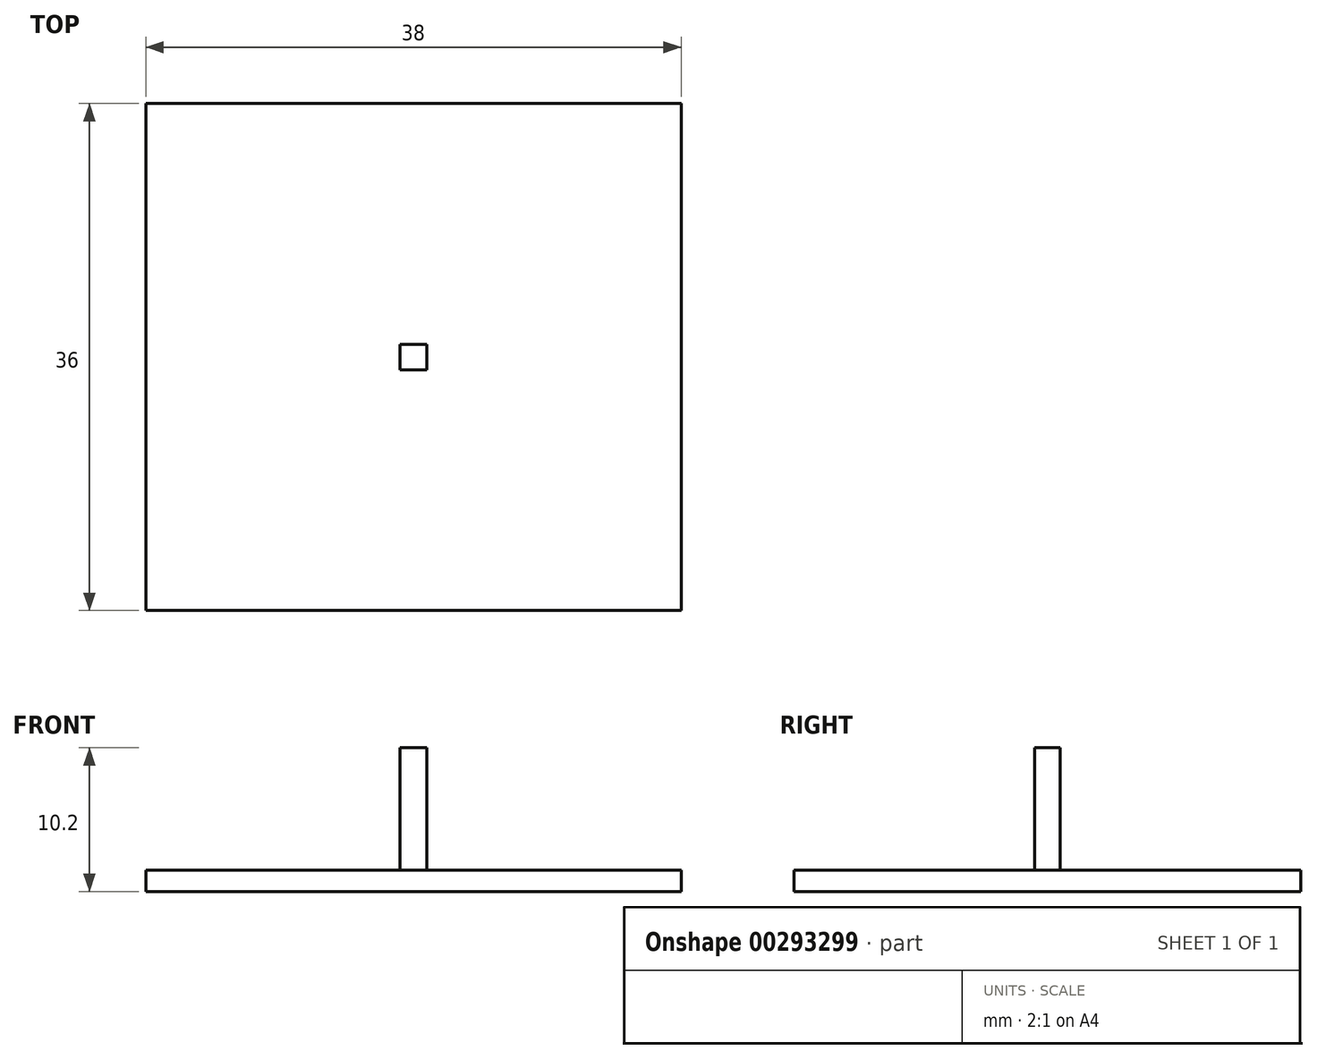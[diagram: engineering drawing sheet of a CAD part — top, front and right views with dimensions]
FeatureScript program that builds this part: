
annotation { "Feature Type Name" : "Feature", "Feature Type Description" : "" }
export const myFeature = defineFeature(function(context is Context, id is Id, definition is map)
    precondition{}
    {
        {
            var Q0;
            Q0=qCreatedBy(makeId("Top.planeOp"),FACE);
            var sketch = newSketch(context, id + "F0", { "sketchPlane" : qUnion([Q0])});
            skLineSegment(sketch, "E0.bottom", {"start": v(19, 18) * mm, "end": v(-19, 18) * mm});
            skLineSegment(sketch, "E0.top", {"start": v(19, -18) * mm, "end": v(-19, -18) * mm});
            skLineSegment(sketch, "E0.left", {"start": v(19, 18) * mm, "end": v(19, -18) * mm});
            skLineSegment(sketch, "E0.right", {"start": v(-19, 18) * mm, "end": v(-19, -18) * mm});
            skPoint(sketch, "E0.middle", {"position": v(0, 0) * mm});
            skSolve(sketch);
        }
        {
            var Q0;
            Q0 = qSketchRegion(id + "F0", true);
            extrude(context, id + "F1", {"entities" : qUnion([Q0]), "depth" : 1.5 * mm});
        }
        {
            var Q0;
            Q0=makeQuery(id+"F1.opExtrude","CAP_FACE",FACE,{"disambiguationData":[OSD([sQuery(id+"F0.wireOp",EDGE,"E0.bottom"),sQuery(id+"F0.wireOp",EDGE,"E0.top"),sQuery(id+"F0.wireOp",EDGE,"E0.left"),sQuery(id+"F0.wireOp",EDGE,"E0.right")])],"isStart":false});
            var sketch = newSketch(context, id + "F2", { "sketchPlane" : qUnion([Q0])});
            skLineSegment(sketch, "E1.bottom", {"start": v(17.71, 16.73) * mm, "end": v(-17.71, 16.73) * mm});
            skLineSegment(sketch, "E1.top", {"start": v(17.71, -16.73) * mm, "end": v(-17.71, -16.73) * mm});
            skLineSegment(sketch, "E1.left", {"start": v(17.71, 16.73) * mm, "end": v(17.71, -16.73) * mm});
            skLineSegment(sketch, "E1.right", {"start": v(-17.71, 16.73) * mm, "end": v(-17.71, -16.73) * mm});
            skPoint(sketch, "E1.middle", {"position": v(0, 0) * mm});
            skLineSegment(sketch, "E2.bottom", {"start": v(0.95, 16.73) * mm, "end": v(-0.95, 16.73) * mm});
            skLineSegment(sketch, "E2.top", {"start": v(0.95, -16.73) * mm, "end": v(-0.95, -16.73) * mm});
            skLineSegment(sketch, "E2.left", {"start": v(0.95, 16.73) * mm, "end": v(0.95, -16.73) * mm});
            skLineSegment(sketch, "E2.right", {"start": v(-0.95, 16.73) * mm, "end": v(-0.95, -16.73) * mm});
            skLineSegment(sketch, "E3.bottom", {"start": v(17.71, 0.9) * mm, "end": v(-17.71, 0.9) * mm});
            skLineSegment(sketch, "E3.top", {"start": v(17.71, -0.9) * mm, "end": v(-17.71, -0.9) * mm});
            skLineSegment(sketch, "E3.left", {"start": v(17.71, 0.9) * mm, "end": v(17.71, -0.9) * mm});
            skLineSegment(sketch, "E3.right", {"start": v(-17.71, 0.9) * mm, "end": v(-17.71, -0.9) * mm});
            skSolve(sketch);
        }
        {
            var Q0;
            {var subQ5=sQuery(id+"F2.wireOp",EDGE,"E3.right");Q0=makeQuery(id+"F2.imprint","IMPRINT",FACE,{"disambiguationData":[TD([[makeQuery(id+"F2.imprint","IMPRINT",EDGE,{"derivedFrom":subQ5}),1.0]])]});}
            var Q1;
            {var subQ5=sQuery(id+"F2.wireOp",EDGE,"E3.left");Q1=makeQuery(id+"F2.imprint","IMPRINT",FACE,{"disambiguationData":[TD([[makeQuery(id+"F2.imprint","IMPRINT",EDGE,{"derivedFrom":subQ5}),-1.0]])]});}
            var Q2;
            {var subQ0=sQuery(id+"F2.wireOp",EDGE,"E3.bottom");var subQ1=sQuery(id+"F2.wireOp",EDGE,"E2.left");var subQ2=makeQuery(id+"F2.imprint","INTERSECT",VERTEX,{"derivedFrom":[subQ1,subQ0]});Q2=makeQuery(id+"F2.imprint","IMPRINT",FACE,{"disambiguationData":[TD([[makeQuery(id+"F2.imprint","IMPRINT",EDGE,{"disambiguationData":[TD([[subQ2,-1.0]])],"derivedFrom":subQ1}),-1.0]])]});}
            var Q3;
            {var subQ0=sQuery(id+"F2.wireOp",EDGE,"E2.bottom");Q3=makeQuery(id+"F2.imprint","IMPRINT",FACE,{"disambiguationData":[TD([[makeQuery(id+"F2.imprint","IMPRINT",EDGE,{"derivedFrom":subQ0}),1.0]])]});}
            var Q4;
            {var subQ0=sQuery(id+"F2.wireOp",EDGE,"E2.top");Q4=makeQuery(id+"F2.imprint","IMPRINT",FACE,{"disambiguationData":[TD([[makeQuery(id+"F2.imprint","IMPRINT",EDGE,{"derivedFrom":subQ0}),-1.0]])]});}
            var Q5;
            {var subQ1=sQuery(id+"F2.wireOp",EDGE,"E2.bottom");Q5=makeQuery(id+"F2.imprint","IMPRINT",FACE,{"disambiguationData":[TD([[makeQuery(id+"F2.imprint","IMPRINT",EDGE,{"derivedFrom":subQ1}),-1.0]])]});}
            extrude(context, id + "F3", {"entities" : qUnion([Q0, Q1, Q2, Q3, Q4, Q5]), "operationType" : NewBodyOperationType.ADD, "depth" : 8.7 * mm});
        }
    });
